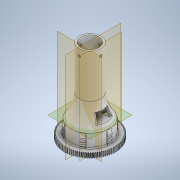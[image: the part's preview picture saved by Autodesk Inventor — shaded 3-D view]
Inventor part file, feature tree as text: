
AUTODESK INVENTOR PART (.ipt)
format: ipt  version: 2022.3 (Build 263350000, 350)  size: 3,565,056 bytes
history: native  units: mm
features: revolve x12, sketch x9, extrude x7, plane x4, hole x3, pattern_circular x2, mirror x2, other x2, fillet x1, projected_geometry x1, reference x1
ambient origin geometry x8: Origin, YZ Plane, XZ Plane, XY Plane, X Axis, Y Axis, Z Axis, Center Point
bodies: Solid1 (feature_tree)
feature tree (44):
  extrude  "Extrusion1"  Depth=4.0mm
  sketch  "Sketch2"  dims[d2=40.0mm d3=0.0mm d4=88.0mm]
  revolve  "Revolution1"  [1 undecoded]
  plane  "Work Plane1"
  extrude  "Extrusion2"  Depth=100.0mm
  sketch  "Sketch18"  dims[d5=50.0mm d8=100.0mm]
  extrude  "Extrusion11"  Depth=100.0mm
  extrude  "Extrusion12"  Depth=100.0mm
  extrude  "Extrusion13"  [1 undecoded]
  pattern_circular  "Circular Pattern2"  [2 undecoded]
  revolve  "Revolution4"  [1 undecoded]
  plane  "Work Plane3"
  plane  "Work Plane4"
  hole  "Hole5"  [1 undecoded]
  hole  "Hole6"  [1 undecoded]
  mirror  "Mirror1"
  mirror  "Mirror2"
  extrude  "Extrusion14"  TaperAngle=0.0deg  [1 undecoded]
  fillet  "Fillet4"  Radius=4.0mm
  extrude  "Extrusion15"  Depth=10.0mm
  plane  "Work Plane5"
  sketch  "Sketch24"  dims[d17=75.0mm d18=5.0mm d19=15.0mm d20=5.2mm d21=5.0mm d22=0.0mm d79=0.0mm d106=4.0mm d107=10.0mm d108=30.0mm d109=0.0mm d110=10.0mm d111=30.0mm d112=0.0mm d113=1.0mm d114=10.0mm d115=1.0mm d116=3.0mm d117=1.0mm d118=5.0mm d119=1.0mm d120=4.0mm d121=1.0mm d122=5.0mm d123=10.0mm d124=90.0deg d131=10.0mm d132=0.0mm d133=1.0mm d134=3.0mm d135=60.0mm d136=360.0deg d138=2.0mm d139=5.0mm d140=2.0mm d141=5.0mm d142=90.0deg d143=25.0mm d144=25.0mm d145=30.0mm d146=3.4mm d147=6.0mm d148=5.9mm d149=2.0mm d150=90.0deg d151=4.2mm d152=0.0mm d153=30.0mm d154=180.0deg d155=3.4mm d156=6.0mm d157=5.9mm d158=2.0mm d159=90.0deg d160=4.2mm d161=0.0mm d162=10.0mm d163=0.0mm d164=2.27mm d165=4.0mm d166=10.0mm d167=0.0mm d168=6.6mm d179=210.0deg d180=150.0deg d181=10.0mm d182=10.0mm d183=90.0deg d184=5.0mm d185=2.0mm d186=2.2mm d187=6.0mm d188=3.1mm d189=4.1mm d190=90.0deg d191=0.9mm d192=0.0mm d193=20.0mm d194=90.0deg d196=20.0mm d197=20.0mm d198=15.0mm d199=10.0mm d200=120.0deg d201=60.0deg d202=10.0mm d203=10.0mm d204=10.0mm d205=1.0mm d206=5.0mm d207=2.0mm d208=5.0mm d209=1.0mm d210=210.0deg d211=35.77925mm d212=27.052603mm d213=20.071286mm d214=11.34464mm d125=0.872665mm d126=0.872665mm d137=14.3117mm]
  revolve  "Revolution5"  [1 undecoded]
  revolve  "Revolution6"  [1 undecoded]
  revolve  "Revolution7"  [1 undecoded]
  hole  "Hole8"  [1 undecoded]
  pattern_circular  "Circular Pattern4"  [2 undecoded]
  revolve  "Revolution8"  [1 undecoded]
  revolve  "Revolution9"  [1 undecoded]
  revolve  "Revolution10"  [1 undecoded]
  revolve  "Revolution11"  [1 undecoded]
  revolve  "Revolution12"  [1 undecoded]
  revolve  "Revolution13"  [1 undecoded]
  revolve  "Revolution14"  [1 undecoded]
  sketch  "Sketch1"  dims[d0=80.0mm d1=4.0mm]
  sketch  "Sketch19"  dims[d9=25.0mm d10=100.0mm]
  sketch  "Sketch20"  dims[d11=4.0mm d12=100.0mm]
  sketch  "Sketch21"  dims[d13=360.0deg d14=-45.0mm]
  sketch  "Sketch22"  dims[d15=5.0mm]
  sketch  "Sketch23"  dims[d16=75.0mm]
  projected_geometry  "Projected Loop3"
  reference  "Reference1"
  other  "v3.0.iam"
  other  "Spur Gear (95 teeth):1"
note: 21 required parameter values undecoded (feature->parameter linkage not recoverable at this tier; creation-order binding heuristic only, values carry confidence <= 0.55)